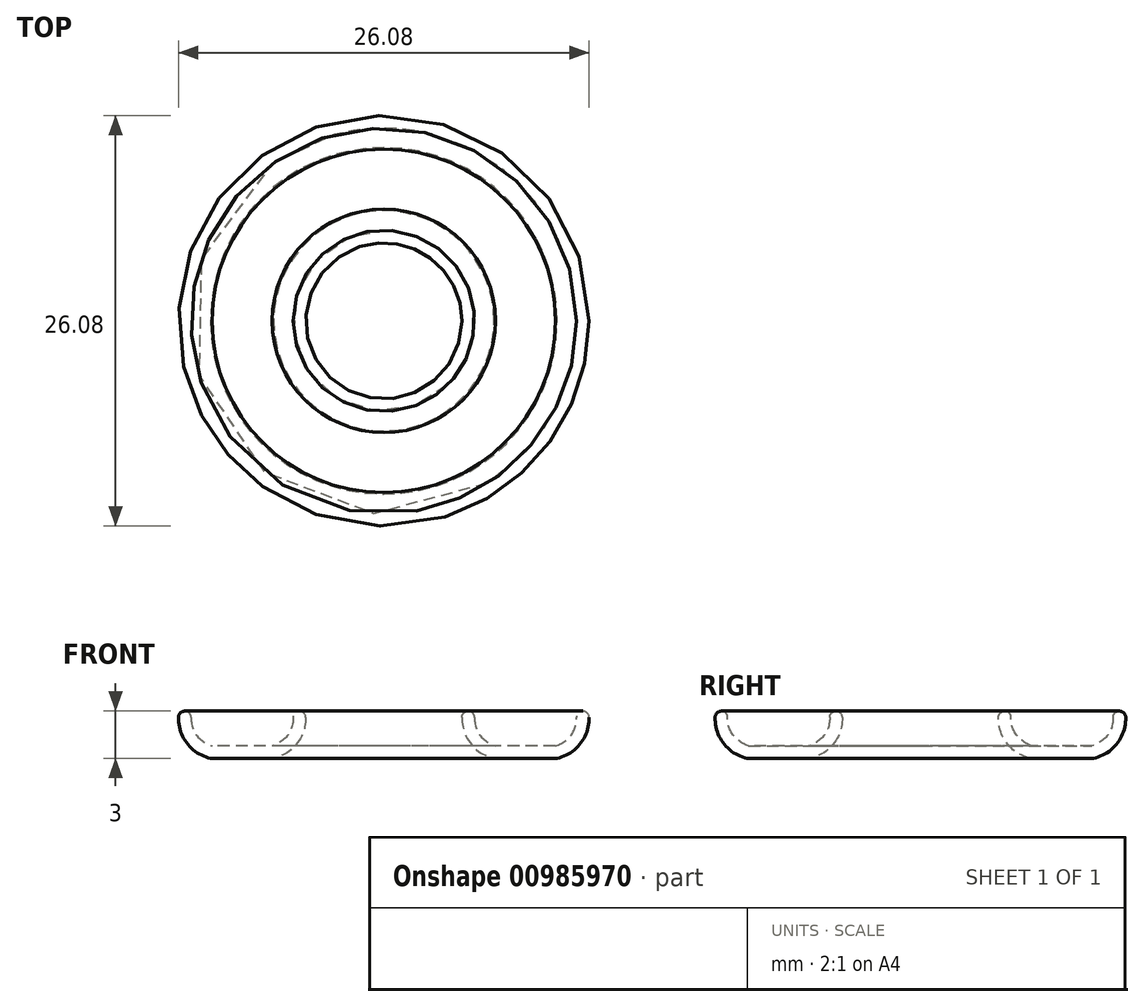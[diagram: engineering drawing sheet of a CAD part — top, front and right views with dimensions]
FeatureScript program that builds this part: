
annotation { "Feature Type Name" : "Feature", "Feature Type Description" : "" }
export const myFeature = defineFeature(function(context is Context, id is Id, definition is map)
    precondition{}
    {
        {
            var Q0;
            Q0=qCreatedBy(makeId("Front.planeOp"),FACE);
            var sketch = newSketch(context, id + "F0", { "sketchPlane" : qUnion([Q0])});
            skLineSegment(sketch, "E0", {"start": v(0, 21.94) * mm, "end": v(0, -25.46) * mm, "construction": true});
            skLineSegment(sketch, "E1", {"start": v(7, 0) * mm, "end": v(11, 0) * mm});
            skLineSegment(sketch, "E2", {"start": v(5, 3) * mm, "end": v(13, 3) * mm});
            skArc(sketch, "E3", {"start": v(5, 3) * mm, "mid": v(5.4, 1.1) * mm, "end": v(7, 0) * mm});
            skArc(sketch, "E4", {"start": v(11, 0) * mm, "mid": v(12.6, 1.1) * mm, "end": v(13, 3) * mm});
            skArc(sketch, "E5.0", {"start": v(10.9, 0.8) * mm, "mid": v(12, 1.64) * mm, "end": v(12.18, 3) * mm});
            skLineSegment(sketch, "E5.1", {"start": v(7.1, 0.8) * mm, "end": v(10.9, 0.8) * mm});
            skArc(sketch, "E5.2", {"start": v(5.82, 3) * mm, "mid": v(6, 1.64) * mm, "end": v(7.1, 0.8) * mm});
            skSolve(sketch);
        }
        {
            var Q0;
            Q0=makeQuery(id+"F0.imprint","IMPRINT",FACE,{"disambiguationData":[TD([[makeQuery(id+"F0.imprint","IMPRINT",EDGE,{"derivedFrom":sQuery(id+"F0.wireOp",EDGE,"E1")}),1.0]])]});
            var Q1;
            Q1=sQuery(id+"F0.wireOp",EDGE,"E0");
            revolve(context, id + "F1", {"surfaceOperationType" : NewSurfaceOperationType.NEW, "entities" : qUnion([Q0]), "axis" : qUnion([Q1]), "revolveType" : RevolveType.FULL});
        }
        {
            var Q0;
            Q0=makeQuery(id+"F1.opRevolve","SWEPT_EDGE",EDGE,{"disambiguationData":[OSD([sQuery(id+"F0.wireOp",EDGE,"E2"),sQuery(id+"F0.wireOp",EDGE,"E5.0")])]});
            var Q1;
            Q1=makeQuery(id+"F1.opRevolve","SWEPT_EDGE",EDGE,{"disambiguationData":[OSD([sQuery(id+"F0.wireOp",EDGE,"E2"),sQuery(id+"F0.wireOp",EDGE,"E5.2")])]});
            var Q2;
            Q2=makeQuery(id+"F1.opRevolve","SWEPT_EDGE",EDGE,{"disambiguationData":[OSD([sQuery(id+"F0.wireOp",EDGE,"E2"),sQuery(id+"F0.wireOp",EDGE,"E3")])]});
            var Q3;
            Q3=makeQuery(id+"F1.opRevolve","SWEPT_EDGE",EDGE,{"disambiguationData":[OSD([sQuery(id+"F0.wireOp",EDGE,"E2"),sQuery(id+"F0.wireOp",EDGE,"E4")])]});
            fillet(context, id + "F2", {"entities" : qUnion([Q0, Q1, Q2, Q3]), "radius" : .4 * mm, "tangentPropagation" : true, "allowEdgeOverflow" : false});
        }
    });
